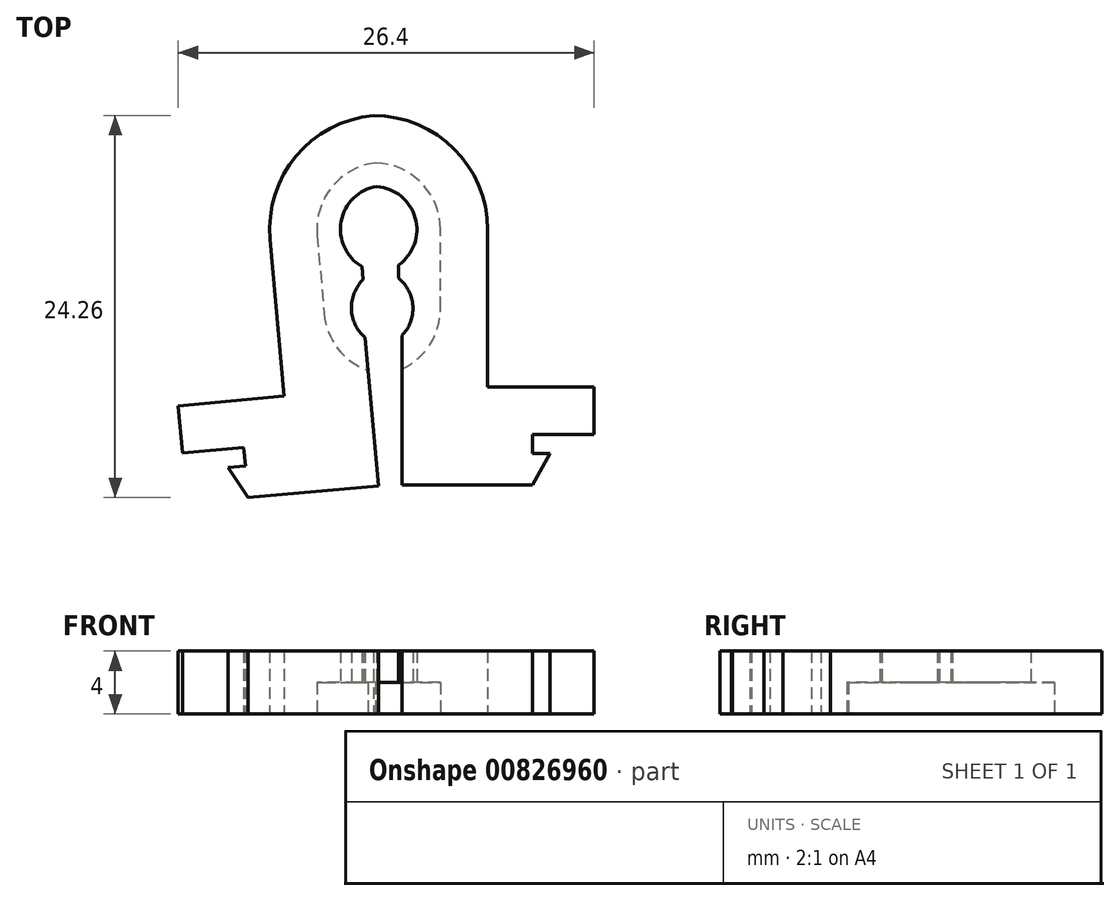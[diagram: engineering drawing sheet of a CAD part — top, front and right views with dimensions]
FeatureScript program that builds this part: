
annotation { "Feature Type Name" : "Feature", "Feature Type Description" : "" }
export const myFeature = defineFeature(function(context is Context, id is Id, definition is map)
    precondition{}
    {
        {
            var Q0;
            Q0=qCreatedBy(makeId("Top.planeOp"),FACE);
            var sketch = newSketch(context, id + "F0", { "sketchPlane" : qUnion([Q0])});
            skArc(sketch, "E0", {"start": v(1.6, -2.24) * mm, "mid": v(2.62, 0.84) * mm, "end": v(0, 2.75) * mm});
            skArc(sketch, "E1.0", {"start": v(4.25, 0) * mm, "mid": v(3, 3) * mm, "end": v(0, 4.25) * mm});
            skLineSegment(sketch, "E2", {"start": v(4.25, 0) * mm, "end": v(4.25, -2.5) * mm});
            skArc(sketch, "E3.MirrorCS", {"start": v(4.25, -5) * mm, "mid": v(3, -8) * mm, "end": v(0, -9.25) * mm});
            skLineSegment(sketch, "E4.MirrorCS", {"start": v(4.25, -5) * mm, "end": v(4.25, -2.5) * mm});
            skLineSegment(sketch, "E5.2", {"start": v(7.25, -5) * mm, "end": v(7.25, -2.5) * mm});
            skLineSegment(sketch, "E5.3", {"start": v(7.25, 0) * mm, "end": v(7.25, -2.5) * mm});
            skArc(sketch, "E5.4", {"start": v(7.25, 0) * mm, "mid": v(5.13, 5.13) * mm, "end": v(0, 7.25) * mm});
            skLineSegment(sketch, "E6", {"start": v(7.25, -5) * mm, "end": v(7.25, -10) * mm});
            skLineSegment(sketch, "E7", {"start": v(7.25, -10) * mm, "end": v(14, -10) * mm});
            skLineSegment(sketch, "E8", {"start": v(14, -10) * mm, "end": v(14, -13) * mm});
            skLineSegment(sketch, "E9", {"start": v(14, -13) * mm, "end": v(10.1, -13) * mm});
            skLineSegment(sketch, "E10", {"start": v(10.1, -13) * mm, "end": v(10.1, -14.2) * mm});
            skLineSegment(sketch, "E11", {"start": v(10.1, -14.2) * mm, "end": v(11.2, -14.2) * mm});
            skLineSegment(sketch, "E12", {"start": v(11.2, -14.2) * mm, "end": v(10.1, -16.2) * mm});
            skLineSegment(sketch, "E13", {"start": v(10.1, -16.2) * mm, "end": v(1.8, -16.2) * mm});
            skLineSegment(sketch, "E14", {"start": v(1.8, -16.2) * mm, "end": v(1.8, -8.85) * mm});
            skLineSegment(sketch, "E15", {"start": v(1.8, -8.85) * mm, "end": v(1.8, -6.73) * mm});
            skLineSegment(sketch, "E16", {"start": v(1.6, -2.24) * mm, "end": v(1.6, -3.08) * mm});
            skArc(sketch, "E17.MirrorCS", {"start": v(1.6, -3.08) * mm, "mid": v(2.5, -4.86) * mm, "end": v(1.8, -6.73) * mm});
            skLineSegment(sketch, "E18", {"start": v(1.8, -16.2) * mm, "end": v(1.05, -16.2) * mm});
            skLineSegment(sketch, "E19", {"start": v(0, 7.25) * mm, "end": v(1.05, -16.2) * mm});
            skLineSegment(sketch, "E20.MirrorCS", {"start": v(-8.14, -15.02) * mm, "end": v(-9.24, -15.12) * mm});
            skLineSegment(sketch, "E21.MirrorCS", {"start": v(0.3, -16.27) * mm, "end": v(1.05, -16.2) * mm});
            skLineSegment(sketch, "E22.MirrorCS", {"start": v(-0.75, -2.34) * mm, "end": v(-0.67, -3.18) * mm});
            skLineSegment(sketch, "E23.MirrorCS", {"start": v(-8.25, -13.82) * mm, "end": v(-8.14, -15.02) * mm});
            skLineSegment(sketch, "E24.MirrorCS", {"start": v(-0.35, -8.95) * mm, "end": v(-0.54, -6.84) * mm});
            skArc(sketch, "E25.MirrorCS", {"start": v(-0.75, -2.34) * mm, "mid": v(-2.03, 0.63) * mm, "end": v(0.4, 2.77) * mm});
            skLineSegment(sketch, "E26.MirrorCS", {"start": v(-12.4, -11.18) * mm, "end": v(-12.13, -14.17) * mm});
            skArc(sketch, "E27.MirrorCS", {"start": v(-3.14, -5.33) * mm, "mid": v(-1.63, -8.21) * mm, "end": v(1.48, -9.18) * mm});
            skArc(sketch, "E28.MirrorCS", {"start": v(-3.58, -0.35) * mm, "mid": v(-2.61, 2.75) * mm, "end": v(0.27, 4.26) * mm});
            skLineSegment(sketch, "E29.MirrorCS", {"start": v(-6.13, -5.6) * mm, "end": v(-6.35, -3.1) * mm});
            skLineSegment(sketch, "E30.MirrorCS", {"start": v(-7.96, -17) * mm, "end": v(0.3, -16.27) * mm});
            skArc(sketch, "E31.MirrorCS", {"start": v(-6.57, -0.62) * mm, "mid": v(-4.92, 4.68) * mm, "end": v(0, 7.25) * mm});
            skLineSegment(sketch, "E32.MirrorCS", {"start": v(-9.24, -15.12) * mm, "end": v(-7.96, -17) * mm});
            skArc(sketch, "E33.MirrorCS", {"start": v(-0.67, -3.18) * mm, "mid": v(-1.4, -5.04) * mm, "end": v(-0.54, -6.84) * mm});
            skLineSegment(sketch, "E34.MirrorCS", {"start": v(-3.58, -0.35) * mm, "end": v(-3.36, -2.84) * mm});
            skLineSegment(sketch, "E35.MirrorCS", {"start": v(-12.13, -14.17) * mm, "end": v(-8.25, -13.82) * mm});
            skLineSegment(sketch, "E36.MirrorCS", {"start": v(-3.14, -5.33) * mm, "end": v(-3.36, -2.84) * mm});
            skLineSegment(sketch, "E37.MirrorCS", {"start": v(0.3, -16.27) * mm, "end": v(-0.35, -8.95) * mm});
            skLineSegment(sketch, "E38.MirrorCS", {"start": v(-6.57, -0.62) * mm, "end": v(-6.35, -3.1) * mm});
            skLineSegment(sketch, "E39.MirrorCS", {"start": v(-6.13, -5.6) * mm, "end": v(-5.68, -10.58) * mm});
            skLineSegment(sketch, "E40.MirrorCS", {"start": v(-5.68, -10.58) * mm, "end": v(-12.4, -11.18) * mm});
            skSolve(sketch);
        }
        {
            var Q0;
            Q0=makeQuery(id+"F0.imprint","IMPRINT",FACE,{"disambiguationData":[TD([[makeQuery(id+"F0.imprint","IMPRINT",EDGE,{"derivedFrom":sQuery(id+"F0.wireOp",EDGE,"E1.0")}),-1.0]])]});
            var Q1;
            Q1=makeQuery(id+"F0.imprint","IMPRINT",FACE,{"disambiguationData":[TD([[makeQuery(id+"F0.imprint","IMPRINT",EDGE,{"derivedFrom":sQuery(id+"F0.wireOp",EDGE,"E20.MirrorCS")}),1.0]])]});
            extrude(context, id + "F1", {"entities" : qUnion([Q0, Q1]), "depth" : 4 * mm, "offsetDistance" : 25 * mm, "symmetric" : true});
        }
        {
            var Q0;
            {var subQ1=sQuery(id+"F0.wireOp",EDGE,"E22.MirrorCS");Q0=makeQuery(id+"F0.imprint","IMPRINT",FACE,{"disambiguationData":[TD([[makeQuery(id+"F0.imprint","IMPRINT",EDGE,{"derivedFrom":subQ1}),-1.0]])]});}
            var Q1;
            {var subQ3=sQuery(id+"F0.wireOp",EDGE,"E2");Q1=makeQuery(id+"F0.imprint","IMPRINT",FACE,{"disambiguationData":[TD([[makeQuery(id+"F0.imprint","IMPRINT",EDGE,{"derivedFrom":subQ3}),-1.0]])]});}
            extrude(context, id + "F2", {"entities" : qUnion([Q0, Q1]), "operationType" : NewBodyOperationType.ADD, "depth" : 2 * mm, "offsetDistance" : 25 * mm});
        }
    });
